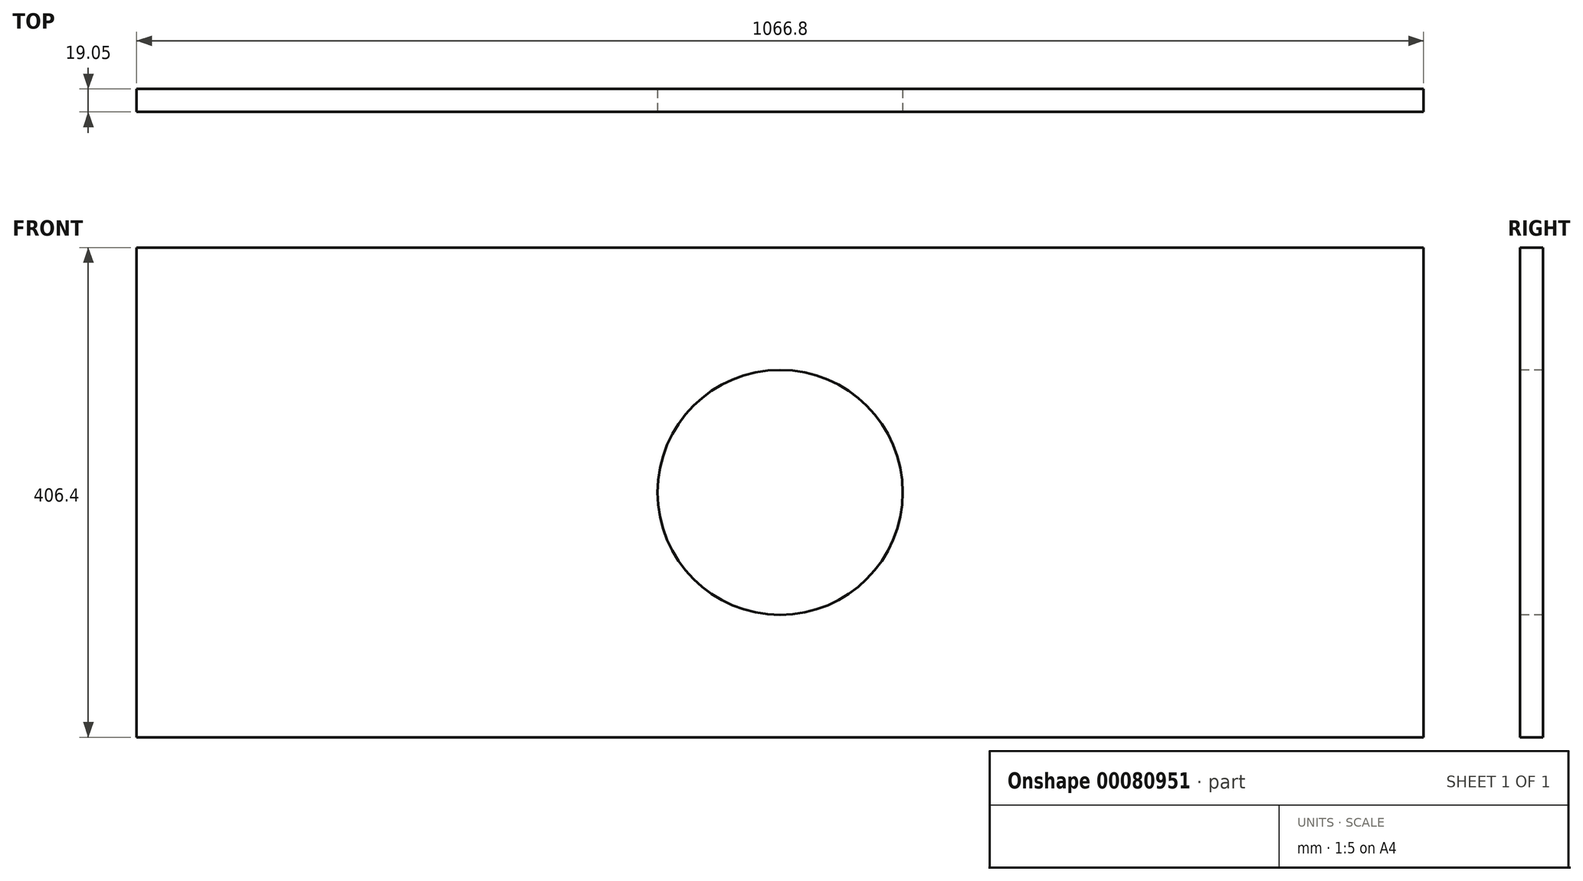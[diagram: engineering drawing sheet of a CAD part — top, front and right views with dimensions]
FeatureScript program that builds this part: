
annotation { "Feature Type Name" : "Feature", "Feature Type Description" : "" }
export const myFeature = defineFeature(function(context is Context, id is Id, definition is map)
    precondition{}
    {
        {
            var Q0;
            Q0=qCreatedBy(makeId("Front.planeOp"),FACE);
            var sketch = newSketch(context, id + "F0", { "sketchPlane" : qUnion([Q0])});
            skLineSegment(sketch, "E0.bottom", {"start": v(-533.4, 203.2) * mm, "end": v(533.4, 203.2) * mm});
            skLineSegment(sketch, "E0.top", {"start": v(-533.4, -203.2) * mm, "end": v(533.4, -203.2) * mm});
            skLineSegment(sketch, "E0.left", {"start": v(-533.4, 203.2) * mm, "end": v(-533.4, -203.2) * mm});
            skLineSegment(sketch, "E0.right", {"start": v(533.4, 203.2) * mm, "end": v(533.4, -203.2) * mm});
            skCircle(sketch, "E1", {"center": v(0, 0) * mm, "radius": 101.6 * mm});
            skLineSegment(sketch, "E2", {"start": v(0, 203.2) * mm, "end": v(0, 0) * mm, "construction": true});
            skLineSegment(sketch, "E3", {"start": v(0, 0) * mm, "end": v(-533.4, 0) * mm, "construction": true});
            skSolve(sketch);
        }
        {
            var Q0;
            Q0=sQuery(id+"F0.wireOp",EDGE,"E1");
            var Q1;
            Q1=sQuery(id+"F0.wireOp",EDGE,"E0.right");
            var Q2;
            Q2=sQuery(id+"F0.wireOp",EDGE,"E0.left");
            var Q3;
            Q3=sQuery(id+"F0.wireOp",EDGE,"E0.bottom");
            var Q4;
            Q4=sQuery(id+"F0.wireOp",EDGE,"E0.top");
            extrude(context, id + "F1", {"bodyType" : ToolBodyType.SURFACE, "surfaceEntities" : qUnion([Q0, Q1, Q2, Q3, Q4]), "depth" : 19.05 * mm});
        }
    });
